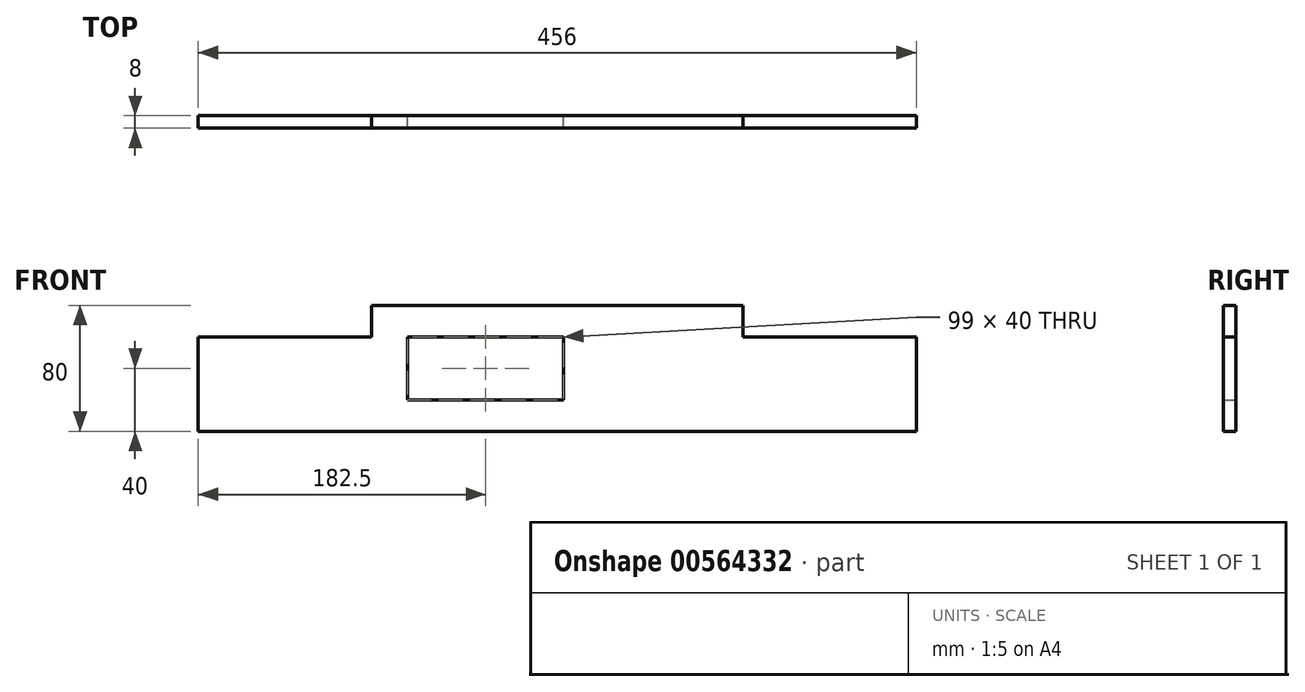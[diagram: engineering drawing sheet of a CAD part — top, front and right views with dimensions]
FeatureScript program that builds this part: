
annotation { "Feature Type Name" : "Feature", "Feature Type Description" : "" }
export const myFeature = defineFeature(function(context is Context, id is Id, definition is map)
    precondition{}
    {
        {
            var Q0;
            Q0=qCreatedBy(makeId("Front.planeOp"),FACE);
            var sketch = newSketch(context, id + "F0", { "sketchPlane" : qUnion([Q0])});
            skLineSegment(sketch, "E0.bottom", {"start": v(0, 40) * mm, "end": v(-228, 40) * mm});
            skLineSegment(sketch, "E0.top", {"start": v(0, -40) * mm, "end": v(-228, -40) * mm});
            skLineSegment(sketch, "E0.left", {"start": v(0, 40) * mm, "end": v(0, -40) * mm});
            skLineSegment(sketch, "E0.right", {"start": v(-228, 40) * mm, "end": v(-228, -40) * mm});
            skLineSegment(sketch, "E1.MirrorCS", {"start": v(0, 40) * mm, "end": v(228, 40) * mm});
            skLineSegment(sketch, "E2.MirrorCS", {"start": v(228, 40) * mm, "end": v(228, -40) * mm});
            skLineSegment(sketch, "E3.MirrorCS", {"start": v(0, -40) * mm, "end": v(228, -40) * mm});
            skLineSegment(sketch, "E4.bottom", {"start": v(4, -20) * mm, "end": v(-95, -20) * mm});
            skLineSegment(sketch, "E4.top", {"start": v(4, 20) * mm, "end": v(-95, 20) * mm});
            skLineSegment(sketch, "E4.left", {"start": v(4, -20) * mm, "end": v(4, 0) * mm});
            skLineSegment(sketch, "E4.right", {"start": v(-95, -20) * mm, "end": v(-95, 20) * mm});
            skPoint(sketch, "E4.middle", {"position": v(0, 0) * mm});
            skLineSegment(sketch, "E5", {"start": v(4, 0) * mm, "end": v(4, 20) * mm});
            skPoint(sketch, "E6", {"position": v(-228, 0) * mm});
            skSolve(sketch);
        }
        {
            var Q0;
            {var subQ0=sQuery(id+"F0.wireOp",EDGE,"E1.MirrorCS");Q0=makeQuery(id+"F0.imprint","IMPRINT",FACE,{"disambiguationData":[TD([[makeQuery(id+"F0.imprint","IMPRINT",EDGE,{"derivedFrom":subQ0}),-1.0]])]});}
            var Q1;
            {var subQ4=sQuery(id+"F0.wireOp",EDGE,"E0.bottom");Q1=makeQuery(id+"F0.imprint","IMPRINT",FACE,{"disambiguationData":[TD([[makeQuery(id+"F0.imprint","IMPRINT",EDGE,{"derivedFrom":subQ4}),1.0]])]});}
            extrude(context, id + "F1", {"entities" : qUnion([Q0, Q1]), "depth" : 8 * mm, "offsetDistance" : 25 * mm});
        }
        {
            var Q0;
            Q0=makeQuery(id+"F1.opExtrude","CAP_FACE",FACE,{"disambiguationData":[OSD([sQuery(id+"F0.wireOp",EDGE,"E0.bottom"),sQuery(id+"F0.wireOp",EDGE,"E0.top"),sQuery(id+"F0.wireOp",EDGE,"E0.right"),sQuery(id+"F0.wireOp",EDGE,"E1.MirrorCS"),sQuery(id+"F0.wireOp",EDGE,"E2.MirrorCS"),sQuery(id+"F0.wireOp",EDGE,"E3.MirrorCS"),sQuery(id+"F0.wireOp",EDGE,"E4.bottom"),sQuery(id+"F0.wireOp",EDGE,"E4.top"),sQuery(id+"F0.wireOp",EDGE,"E4.left"),sQuery(id+"F0.wireOp",EDGE,"E4.right"),sQuery(id+"F0.wireOp",EDGE,"E5")])],"isStart":false});
            var sketch = newSketch(context, id + "F2", { "sketchPlane" : qUnion([Q0])});
            skLineSegment(sketch, "E7.bottom", {"start": v(-228, 40) * mm, "end": v(-118, 40) * mm});
            skLineSegment(sketch, "E7.top", {"start": v(-228, 20) * mm, "end": v(-118, 20) * mm});
            skLineSegment(sketch, "E7.left", {"start": v(-228, 40) * mm, "end": v(-228, 20) * mm});
            skLineSegment(sketch, "E7.right", {"start": v(-118, 40) * mm, "end": v(-118, 20) * mm});
            skLineSegment(sketch, "E8.MirrorCS", {"start": v(118, 40) * mm, "end": v(118, 20) * mm});
            skLineSegment(sketch, "E9.MirrorCS", {"start": v(228, 20) * mm, "end": v(118, 20) * mm});
            skLineSegment(sketch, "E10.MirrorCS", {"start": v(228, 40) * mm, "end": v(228, 20) * mm});
            skLineSegment(sketch, "E11.MirrorCS", {"start": v(228, 40) * mm, "end": v(118, 40) * mm});
            skSolve(sketch);
        }
        {
            var Q0;
            Q0 = qSketchRegion(id + "F2", true);
            extrude(context, id + "F3", {"entities" : qUnion([Q0]), "operationType" : NewBodyOperationType.REMOVE, "oppositeDirection" : true, "depth" : 25 * mm, "offsetDistance" : 25 * mm});
        }
    });
